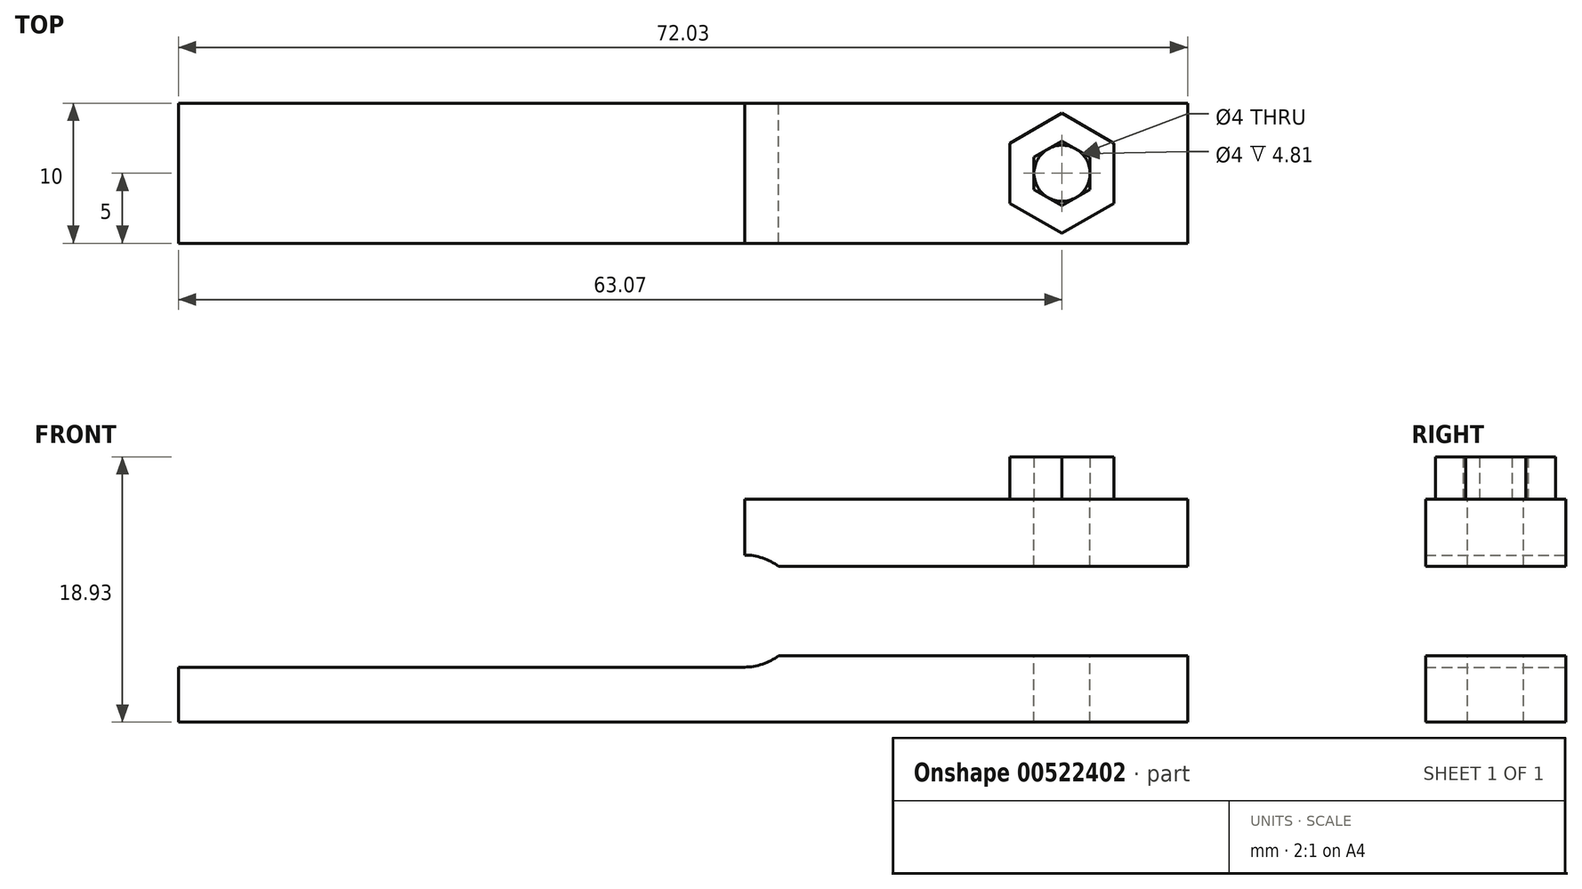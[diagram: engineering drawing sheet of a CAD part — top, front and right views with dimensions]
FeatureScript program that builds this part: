
annotation { "Feature Type Name" : "Feature", "Feature Type Description" : "" }
export const myFeature = defineFeature(function(context is Context, id is Id, definition is map)
    precondition{}
    {
        {
            var Q0;
            Q0=qCreatedBy(makeId("Front.planeOp"),FACE);
            var sketch = newSketch(context, id + "F0", { "sketchPlane" : qUnion([Q0])});
            skCircle(sketch, "E0", {"center": v(0, 0) * mm, "radius": 4 * mm});
            skCircle(sketch, "E1", {"center": v(0, 0) * mm, "radius": 8 * mm});
            skLineSegment(sketch, "E2.bottom", {"start": v(0, -4) * mm, "end": v(-40.42, -4) * mm});
            skLineSegment(sketch, "E2.top", {"start": v(0, -7.93) * mm, "end": v(-40.42, -7.93) * mm});
            skLineSegment(sketch, "E2.left", {"start": v(0, -4) * mm, "end": v(0, -7.93) * mm});
            skLineSegment(sketch, "E2.right", {"start": v(-40.42, -4) * mm, "end": v(-40.42, -7.93) * mm});
            skLineSegment(sketch, "E3.bottom", {"start": v(0, -4) * mm, "end": v(0, -4) * mm});
            skLineSegment(sketch, "E3.top", {"start": v(0, -7.93) * mm, "end": v(0, -7.93) * mm});
            skLineSegment(sketch, "E4.bottom", {"start": v(0, -4) * mm, "end": v(31.6, -4) * mm});
            skLineSegment(sketch, "E4.top", {"start": v(0, -7.93) * mm, "end": v(31.6, -7.93) * mm});
            skLineSegment(sketch, "E4.right", {"start": v(31.6, -4) * mm, "end": v(31.6, -7.93) * mm});
            skLineSegment(sketch, "E5.bottom", {"start": v(0, 4) * mm, "end": v(0, 4) * mm});
            skLineSegment(sketch, "E5.top", {"start": v(0, 8) * mm, "end": v(0, 8) * mm});
            skLineSegment(sketch, "E5.left", {"start": v(0, 4) * mm, "end": v(0, 8) * mm});
            skLineSegment(sketch, "E5.right", {"start": v(0, 4) * mm, "end": v(0, 8) * mm});
            skLineSegment(sketch, "E6.bottom", {"start": v(31.6, 8) * mm, "end": v(0, 8) * mm});
            skLineSegment(sketch, "E6.top", {"start": v(31.6, 4) * mm, "end": v(0, 4) * mm});
            skLineSegment(sketch, "E6.left", {"start": v(31.6, 8) * mm, "end": v(31.6, 4) * mm});
            skLineSegment(sketch, "E6.right", {"start": v(0, 8) * mm, "end": v(0, 4) * mm});
            skLineSegment(sketch, "E7.bottom", {"start": v(2.41, 3.19) * mm, "end": v(31.6, 3.19) * mm});
            skLineSegment(sketch, "E7.top", {"start": v(2.41, 4) * mm, "end": v(31.6, 4) * mm});
            skLineSegment(sketch, "E7.left", {"start": v(2.41, 3.19) * mm, "end": v(2.41, 4) * mm});
            skLineSegment(sketch, "E7.right", {"start": v(31.6, 3.19) * mm, "end": v(31.6, 4) * mm});
            skLineSegment(sketch, "E8.bottom", {"start": v(31.6, -4) * mm, "end": v(2.41, -4) * mm});
            skLineSegment(sketch, "E8.top", {"start": v(31.6, -3.19) * mm, "end": v(2.41, -3.19) * mm});
            skLineSegment(sketch, "E8.left", {"start": v(31.6, -4) * mm, "end": v(31.6, -3.19) * mm});
            skLineSegment(sketch, "E8.right", {"start": v(2.41, -4) * mm, "end": v(2.41, -3.19) * mm});
            skSolve(sketch);
        }
        {
            var Q0;
            {var subQ3=sQuery(id+"F0.wireOp",EDGE,"E6.right");Q0=makeQuery(id+"F0.imprint","IMPRINT",FACE,{"disambiguationData":[TD([[makeQuery(id+"F0.imprint","IMPRINT",EDGE,{"derivedFrom":subQ3}),-1.0]])]});}
            var Q1;
            {var subQ0=sQuery(id+"F0.wireOp",EDGE,"E6.bottom");Q1=makeQuery(id+"F0.imprint","IMPRINT",FACE,{"disambiguationData":[TD([[makeQuery(id+"F0.imprint","IMPRINT",EDGE,{"derivedFrom":subQ0}),1.0]])]});}
            var Q2;
            {var subQ4=sQuery(id+"F0.wireOp",EDGE,"E6.top");Q2=makeQuery(id+"F0.imprint","IMPRINT",FACE,{"disambiguationData":[TD([[makeQuery(id+"F0.imprint","IMPRINT",EDGE,{"derivedFrom":subQ4}),-1.0]])]});}
            var Q3;
            {var subQ5=sQuery(id+"F0.wireOp",EDGE,"E4.right");Q3=makeQuery(id+"F0.imprint","IMPRINT",FACE,{"disambiguationData":[TD([[makeQuery(id+"F0.imprint","IMPRINT",EDGE,{"derivedFrom":subQ5}),-1.0]])]});}
            var Q4;
            {var subQ5=sQuery(id+"F0.wireOp",EDGE,"E2.right");Q4=makeQuery(id+"F0.imprint","IMPRINT",FACE,{"disambiguationData":[TD([[makeQuery(id+"F0.imprint","IMPRINT",EDGE,{"derivedFrom":subQ5}),1.0]])]});}
            var Q5;
            {var subQ5=sQuery(id+"F0.wireOp",EDGE,"E2.left");Q5=makeQuery(id+"F0.imprint","IMPRINT",FACE,{"disambiguationData":[TD([[makeQuery(id+"F0.imprint","IMPRINT",EDGE,{"derivedFrom":subQ5}),-1.0]])]});}
            var Q6;
            {var subQ6=sQuery(id+"F0.wireOp",EDGE,"E4.bottom");Q6=makeQuery(id+"F0.imprint","IMPRINT",FACE,{"disambiguationData":[TD([[makeQuery(id+"F0.imprint","IMPRINT",EDGE,{"derivedFrom":subQ6}),-1.0]])]});}
            var Q7;
            {var subQ5=sQuery(id+"F0.wireOp",EDGE,"E7.left");Q7=makeQuery(id+"F0.imprint","IMPRINT",FACE,{"disambiguationData":[TD([[makeQuery(id+"F0.imprint","IMPRINT",EDGE,{"derivedFrom":subQ5}),-1.0]])]});}
            var Q8;
            {var subQ5=sQuery(id+"F0.wireOp",EDGE,"E7.right");Q8=makeQuery(id+"F0.imprint","IMPRINT",FACE,{"disambiguationData":[TD([[makeQuery(id+"F0.imprint","IMPRINT",EDGE,{"derivedFrom":subQ5}),1.0]])]});}
            var Q9;
            {var subQ5=sQuery(id+"F0.wireOp",EDGE,"E8.right");Q9=makeQuery(id+"F0.imprint","IMPRINT",FACE,{"disambiguationData":[TD([[makeQuery(id+"F0.imprint","IMPRINT",EDGE,{"derivedFrom":subQ5}),-1.0]])]});}
            var Q10;
            {var subQ0=sQuery(id+"F0.wireOp",EDGE,"E4.bottom");Q10=makeQuery(id+"F0.imprint","IMPRINT",FACE,{"disambiguationData":[TD([[makeQuery(id+"F0.imprint","IMPRINT",EDGE,{"derivedFrom":subQ0}),1.0]])]});}
            var Q11;
            {var subQ0=sQuery(id+"F0.wireOp",EDGE,"E6.top");Q11=makeQuery(id+"F0.imprint","IMPRINT",FACE,{"disambiguationData":[TD([[makeQuery(id+"F0.imprint","IMPRINT",EDGE,{"derivedFrom":subQ0}),1.0]])]});}
            var Q12;
            {var subQ5=sQuery(id+"F0.wireOp",EDGE,"E8.left");Q12=makeQuery(id+"F0.imprint","IMPRINT",FACE,{"disambiguationData":[TD([[makeQuery(id+"F0.imprint","IMPRINT",EDGE,{"derivedFrom":subQ5}),1.0]])]});}
            extrude(context, id + "F1", {"entities" : qUnion([Q0, Q1, Q2, Q3, Q4, Q5, Q6, Q7, Q8, Q9, Q10, Q11, Q12]), "endBound" : BoundingType.SYMMETRIC, "depth" : 10 * mm, "offsetDistance" : 25 * mm});
        }
        {
            var Q0;
            Q0=makeQuery(id+"F1.opExtrude","SWEPT_FACE",FACE,{"disambiguationData":[OSD([sQuery(id+"F0.wireOp",EDGE,"E6.bottom")])]});
            var sketch = newSketch(context, id + "F2", { "sketchPlane" : qUnion([Q0])});
            skCircle(sketch, "E9.cCircle", {"center": v(22.65, 0) * mm, "radius": 2 * mm, "construction": true});
            skLineSegment(sketch, "E9.0", {"start": v(24.65, 1.15) * mm, "end": v(24.65, -1.15) * mm});
            skLineSegment(sketch, "E9.1", {"start": v(24.65, -1.15) * mm, "end": v(22.65, -2.3) * mm});
            skLineSegment(sketch, "E9.2", {"start": v(22.65, -2.3) * mm, "end": v(20.65, -1.15) * mm});
            skLineSegment(sketch, "E9.3", {"start": v(20.65, -1.15) * mm, "end": v(20.65, 1.15) * mm});
            skLineSegment(sketch, "E9.4", {"start": v(20.65, 1.15) * mm, "end": v(22.65, 2.3) * mm});
            skLineSegment(sketch, "E9.5", {"start": v(22.65, 2.3) * mm, "end": v(24.65, 1.15) * mm});
            skPoint(sketch, "E9.0.midPoint", {"position": v(24.65, 0) * mm});
            skCircle(sketch, "E10.cCircle", {"center": v(22.65, 0) * mm, "radius": 3.72 * mm, "construction": true});
            skLineSegment(sketch, "E10.0", {"start": v(26.37, 2.15) * mm, "end": v(26.37, -2.15) * mm});
            skLineSegment(sketch, "E10.1", {"start": v(26.37, -2.15) * mm, "end": v(22.65, -4.3) * mm});
            skLineSegment(sketch, "E10.2", {"start": v(22.65, -4.3) * mm, "end": v(18.93, -2.15) * mm});
            skLineSegment(sketch, "E10.3", {"start": v(18.93, -2.15) * mm, "end": v(18.93, 2.15) * mm});
            skLineSegment(sketch, "E10.4", {"start": v(18.93, 2.15) * mm, "end": v(22.65, 4.3) * mm});
            skLineSegment(sketch, "E10.5", {"start": v(22.65, 4.3) * mm, "end": v(26.37, 2.15) * mm});
            skPoint(sketch, "E10.0.midPoint", {"position": v(26.37, 0) * mm});
            skCircle(sketch, "E11", {"center": v(22.65, 0) * mm, "radius": 2 * mm});
            skSolve(sketch);
        }
        {
            var Q0;
            Q0 = qSketchRegion(id + "F2", true);
            extrude(context, id + "F3", {"entities" : qUnion([Q0]), "operationType" : NewBodyOperationType.ADD, "depth" : 3 * mm, "offsetDistance" : 25 * mm});
        }
        {
            var Q0;
            {var subQ0=sQuery(id+"F2.wireOp",EDGE,"E11");var subQ5=makeQuery(id+"F2.imprint","INTERSECT",VERTEX,{"derivedFrom":[sQuery(id+"F2.wireOp",EDGE,"E9.0"),subQ0]});Q0=makeQuery(id+"F2.imprint","IMPRINT",FACE,{"disambiguationData":[TD([[makeQuery(id+"F2.imprint","IMPRINT",EDGE,{"disambiguationData":[TD([[subQ5,-1.0]])],"derivedFrom":subQ0}),1.0]])]});}
            var Q1;
            Q1=sQuery(id+"F2.wireOp",EDGE,"E11");
            extrude(context, id + "F4", {"entities" : qUnion([Q0]), "operationType" : NewBodyOperationType.REMOVE, "surfaceEntities" : qUnion([Q1]), "oppositeDirection" : true, "depth" : 16 * mm, "offsetDistance" : 25 * mm});
        }
    });
